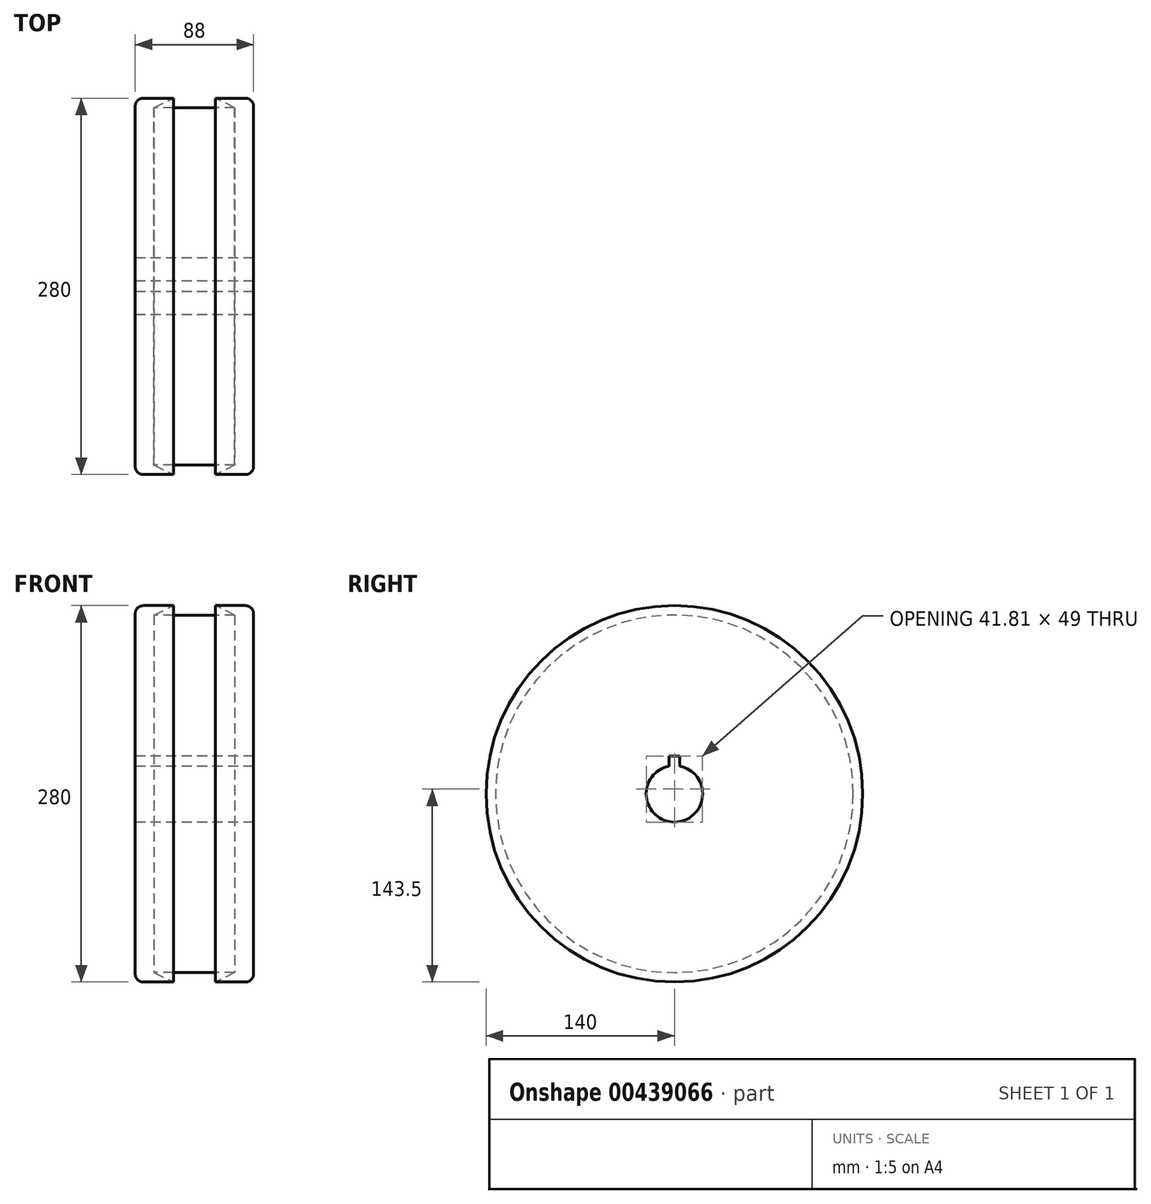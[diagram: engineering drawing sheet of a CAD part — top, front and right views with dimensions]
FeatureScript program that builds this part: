
annotation { "Feature Type Name" : "Feature", "Feature Type Description" : "" }
export const myFeature = defineFeature(function(context is Context, id is Id, definition is map)
    precondition{}
    {
        {
            var Q0;
            Q0=qCreatedBy(makeId("Front.planeOp"),FACE);
            var sketch = newSketch(context, id + "F0", { "sketchPlane" : qUnion([Q0])});
            skLineSegment(sketch, "E0.bottom", {"start": v(-44, 0) * mm, "end": v(44, 0) * mm});
            skLineSegment(sketch, "E0.top", {"start": v(-44, 140) * mm, "end": v(-15.61, 140) * mm});
            skLineSegment(sketch, "E0.left", {"start": v(-44, 0) * mm, "end": v(-44, 140) * mm});
            skLineSegment(sketch, "E0.right", {"start": v(44, 0) * mm, "end": v(44, 140) * mm});
            skLineSegment(sketch, "E1", {"start": v(-30, 133) * mm, "end": v(30, 133) * mm});
            skLineSegment(sketch, "E2", {"start": v(30, 133) * mm, "end": v(15.61, 140) * mm});
            skLineSegment(sketch, "E3", {"start": v(15.61, 140) * mm, "end": v(44, 140) * mm});
            skLineSegment(sketch, "E4", {"start": v(-30, 133) * mm, "end": v(-15.61, 140) * mm});
            skSolve(sketch);
        }
        {
            var Q0;
            Q0=qSketchRegion(id+"F0",true);
            var Q1;
            Q1=sQuery(id+"F0.wireOp",EDGE,"E0.bottom");
            revolve(context, id + "F1", {"entities" : qUnion([Q0]), "axis" : qUnion([Q1]), "revolveType" : RevolveType.FULL});
        }
        {
            var Q0;
            Q0=makeQuery(id+"F1.opRevolve","SWEPT_EDGE",EDGE,{"disambiguationData":[OSD([sQuery(id+"F0.wireOp",EDGE,"E0.top"),sQuery(id+"F0.wireOp",EDGE,"E0.left")])]});
            var Q1;
            Q1=makeQuery(id+"F1.opRevolve","SWEPT_EDGE",EDGE,{"disambiguationData":[OSD([sQuery(id+"F0.wireOp",EDGE,"E0.right"),sQuery(id+"F0.wireOp",EDGE,"E3")])]});
            fillet(context, id + "F2", {"entities" : qUnion([Q0, Q1]), "radius" : 6 * mm, "tangentPropagation" : true, "allowEdgeOverflow" : false});
        }
        {
            var Q0;
            Q0=makeQuery(id+"F1.opRevolve","SWEPT_FACE",FACE,{"disambiguationData":[OSD([sQuery(id+"F0.wireOp",EDGE,"E0.left")])]});
            var sketch = newSketch(context, id + "F3", { "sketchPlane" : qUnion([Q0])});
            skCircle(sketch, "E5", {"center": v(0, 0) * mm, "radius": 21 * mm});
            skLineSegment(sketch, "E6.bottom", {"start": v(-4, 16) * mm, "end": v(4, 16) * mm});
            skLineSegment(sketch, "E6.top", {"start": v(-4, 28) * mm, "end": v(4, 28) * mm});
            skLineSegment(sketch, "E6.left", {"start": v(-4, 16) * mm, "end": v(-4, 28) * mm});
            skLineSegment(sketch, "E6.right", {"start": v(4, 16) * mm, "end": v(4, 28) * mm});
            skSolve(sketch);
        }
        {
            var Q0;
            Q0=qSketchRegion(id+"F3",true);
            extrude(context, id + "F4", {"entities" : qUnion([Q0]), "operationType" : NewBodyOperationType.REMOVE, "oppositeDirection" : true, "depth" : 88 * mm});
        }
    });
